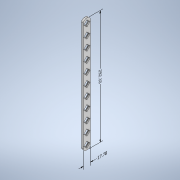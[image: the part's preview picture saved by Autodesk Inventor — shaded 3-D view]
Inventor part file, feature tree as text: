
AUTODESK INVENTOR PART (.ipt)
format: ipt  version: 2020 (Build 240168000, 168)  size: 428,544 bytes
history: native  units: mm
features: chamfer x88, other x3, extrude x2, sketch x2, fillet x1
ambient origin geometry x8: Origin, YZ Plane, XZ Plane, XY Plane, X Axis, Y Axis, Z Axis, Center Point
bodies: Solid1 (feature_tree)
feature tree (96):
  other  "Annotations"
  extrude  "Extrusion1"  Depth=17.78mm
  extrude  "Extrusion2"  Depth=5.0mm TaperAngle=0.0deg
  fillet  "Fillet1"  Radius=7.0mm
  chamfer  "Chamfer1"  Distance=1.0mm Angle=45.0deg
  chamfer  "Chamfer2"  Distance=1.0mm Angle=45.0deg
  chamfer  "Chamfer3"  Distance=1.0mm Angle=45.0deg
  chamfer  "Chamfer4"  Distance=1.0mm Angle=45.0deg
  chamfer  "Chamfer5"  Distance=1.0mm Angle=45.0deg
  chamfer  "Chamfer6"  Distance=1.0mm Angle=45.0deg
  chamfer  "Chamfer7"  Distance=1.0mm Angle=45.0deg
  chamfer  "Chamfer8"  Distance=1.0mm Angle=45.0deg
  chamfer  "Chamfer9"  Distance=1.0mm Angle=45.0deg
  chamfer  "Chamfer10"  Distance=1.0mm Angle=45.0deg
  chamfer  "Chamfer11"  Distance=1.0mm Angle=45.0deg
  chamfer  "Chamfer12"  Distance=1.0mm Angle=45.0deg
  chamfer  "Chamfer13"  Distance=1.0mm Angle=45.0deg
  chamfer  "Chamfer14"  Distance=1.0mm Angle=45.0deg
  chamfer  "Chamfer15"  Distance=1.0mm Angle=45.0deg
  chamfer  "Chamfer16"  Distance=1.0mm Angle=45.0deg
  chamfer  "Chamfer17"  Distance=1.0mm Angle=45.0deg
  chamfer  "Chamfer18"  Distance=1.0mm Angle=45.0deg
  chamfer  "Chamfer19"  Distance=1.0mm Angle=45.0deg
  chamfer  "Chamfer20"  Distance=1.0mm Angle=45.0deg
  chamfer  "Chamfer21"  Distance=1.0mm Angle=45.0deg
  chamfer  "Chamfer22"  Distance=1.0mm Angle=45.0deg
  chamfer  "Chamfer23"  Distance=1.0mm Angle=45.0deg
  chamfer  "Chamfer24"  Distance=1.0mm Angle=45.0deg
  chamfer  "Chamfer25"  Distance=1.0mm Angle=45.0deg
  chamfer  "Chamfer26"  Distance=1.0mm Angle=45.0deg
  chamfer  "Chamfer27"  Distance=1.0mm Angle=45.0deg
  chamfer  "Chamfer28"  Distance=1.0mm Angle=45.0deg
  chamfer  "Chamfer29"  Distance=1.0mm Angle=45.0deg
  chamfer  "Chamfer30"  Distance=1.0mm Angle=45.0deg
  chamfer  "Chamfer31"  Distance=1.0mm Angle=45.0deg
  chamfer  "Chamfer32"  Distance=1.0mm Angle=45.0deg
  chamfer  "Chamfer33"  Distance=1.0mm Angle=45.0deg
  chamfer  "Chamfer34"  Distance=1.0mm Angle=45.0deg
  chamfer  "Chamfer35"  Distance=1.0mm Angle=45.0deg
  chamfer  "Chamfer36"  Distance=1.0mm Angle=45.0deg
  chamfer  "Chamfer37"  Distance=1.0mm Angle=45.0deg
  chamfer  "Chamfer38"  Distance=1.0mm Angle=45.0deg
  chamfer  "Chamfer39"  Distance=1.0mm Angle=45.0deg
  chamfer  "Chamfer40"  Distance=1.0mm Angle=45.0deg
  chamfer  "Chamfer41"  Distance=1.0mm Angle=45.0deg
  chamfer  "Chamfer42"  Distance=1.0mm Angle=45.0deg
  chamfer  "Chamfer43"  Distance=1.0mm Angle=45.0deg
  chamfer  "Chamfer44"  Distance=1.0mm Angle=45.0deg
  chamfer  "Chamfer45"  Distance=1.0mm Angle=45.0deg
  chamfer  "Chamfer46"  Distance=1.0mm Angle=45.0deg
  chamfer  "Chamfer47"  Distance=1.0mm Angle=45.0deg
  chamfer  "Chamfer48"  Distance=1.0mm Angle=45.0deg
  chamfer  "Chamfer49"  Distance=1.0mm Angle=45.0deg
  chamfer  "Chamfer50"  Distance=1.0mm Angle=45.0deg
  chamfer  "Chamfer51"  Distance=1.0mm Angle=45.0deg
  chamfer  "Chamfer52"  Distance=1.0mm Angle=45.0deg
  chamfer  "Chamfer53"  Distance=1.0mm Angle=45.0deg
  chamfer  "Chamfer54"  Distance=1.0mm Angle=45.0deg
  chamfer  "Chamfer55"  Distance=1.0mm Angle=45.0deg
  chamfer  "Chamfer56"  Distance=1.0mm Angle=45.0deg
  chamfer  "Chamfer57"  Distance=1.0mm Angle=45.0deg
  chamfer  "Chamfer58"  Distance=1.0mm Angle=45.0deg
  chamfer  "Chamfer59"  Distance=1.0mm Angle=45.0deg
  chamfer  "Chamfer60"  Distance=1.0mm Angle=45.0deg
  chamfer  "Chamfer61"  Distance=1.0mm Angle=45.0deg
  chamfer  "Chamfer62"  Distance=1.0mm Angle=45.0deg
  chamfer  "Chamfer63"  Distance=1.0mm Angle=45.0deg
  chamfer  "Chamfer64"  Distance=1.0mm Angle=45.0deg
  chamfer  "Chamfer65"  Distance=1.0mm Angle=45.0deg
  chamfer  "Chamfer66"  Distance=1.0mm Angle=45.0deg
  chamfer  "Chamfer67"  Distance=1.0mm Angle=45.0deg
  chamfer  "Chamfer68"  Distance=1.0mm Angle=45.0deg
  chamfer  "Chamfer69"  Distance=1.0mm Angle=45.0deg
  chamfer  "Chamfer70"  Distance=1.0mm Angle=45.0deg
  chamfer  "Chamfer71"  Distance=1.0mm Angle=45.0deg
  chamfer  "Chamfer72"  Distance=1.0mm Angle=45.0deg
  chamfer  "Chamfer73"  Distance=1.0mm Angle=45.0deg
  chamfer  "Chamfer74"  Distance=1.0mm Angle=45.0deg
  chamfer  "Chamfer75"  Distance=1.0mm Angle=45.0deg
  chamfer  "Chamfer76"  Distance=1.0mm Angle=45.0deg
  chamfer  "Chamfer77"  Distance=1.0mm Angle=45.0deg
  chamfer  "Chamfer78"  Distance=1.0mm Angle=45.0deg
  chamfer  "Chamfer79"  Distance=1.0mm Angle=45.0deg
  chamfer  "Chamfer80"  Distance=1.0mm Angle=45.0deg
  chamfer  "Chamfer81"  Distance=1.0mm Angle=45.0deg
  chamfer  "Chamfer82"  Distance=1.0mm Angle=45.0deg
  chamfer  "Chamfer83"  Distance=1.0mm Angle=45.0deg
  chamfer  "Chamfer84"  Distance=1.0mm Angle=45.0deg
  chamfer  "Chamfer85"  Distance=1.0mm Angle=45.0deg
  chamfer  "Chamfer86"  Distance=1.0mm Angle=45.0deg
  chamfer  "Chamfer87"  Distance=1.0mm Angle=45.0deg
  chamfer  "Chamfer88"  Distance=1.0mm Angle=45.0deg
  sketch  "Sketch1"  dims[d0=292.1mm d1=17.78mm]
  sketch  "Sketch2"  dims[d2=5.0mm d3=0.0mm d15=5.0mm d16=0.0mm d17=7.0mm d18=1.0mm d19=2.0mm d20=45.0deg d21=1.0mm d22=2.0mm d23=45.0deg d24=1.0mm d25=2.0mm d26=45.0deg d27=1.0mm d28=2.0mm d29=45.0deg d30=1.0mm d31=2.0mm d32=45.0deg d33=1.0mm d34=2.0mm d35=45.0deg d36=1.0mm d37=2.0mm d38=45.0deg d39=1.0mm d40=2.0mm d41=45.0deg d42=1.0mm d43=2.0mm d44=45.0deg d45=1.0mm d46=2.0mm d47=45.0deg d48=1.0mm d49=2.0mm d50=45.0deg d51=1.0mm d52=2.0mm d53=45.0deg d54=1.0mm d55=2.0mm d56=45.0deg d57=1.0mm d58=2.0mm d59=45.0deg d60=1.0mm d61=2.0mm d62=45.0deg d63=1.0mm d64=2.0mm d65=45.0deg d66=1.0mm d67=2.0mm d68=45.0deg d69=1.0mm d70=2.0mm d71=45.0deg d72=1.0mm d73=2.0mm d74=45.0deg d75=1.0mm d76=2.0mm d77=45.0deg d78=1.0mm d79=2.0mm d80=45.0deg d81=1.0mm d82=2.0mm d83=45.0deg d84=1.0mm d85=2.0mm d86=45.0deg d87=1.0mm d88=2.0mm d89=45.0deg d90=1.0mm d91=2.0mm d92=45.0deg d93=1.0mm d94=2.0mm d95=45.0deg d96=1.0mm d97=2.0mm d98=45.0deg d99=1.0mm d100=2.0mm d101=45.0deg d102=1.0mm d103=2.0mm d104=45.0deg d105=1.0mm d106=2.0mm d107=45.0deg d108=1.0mm d109=2.0mm d110=45.0deg d111=1.0mm d112=2.0mm d113=45.0deg d114=1.0mm d115=2.0mm d116=45.0deg d117=1.0mm d118=2.0mm d119=45.0deg d120=1.0mm d121=2.0mm d122=45.0deg d123=1.0mm d124=2.0mm d125=45.0deg d126=1.0mm d127=2.0mm d128=45.0deg d129=1.0mm d130=2.0mm d131=45.0deg d132=1.0mm d133=2.0mm d134=45.0deg d135=1.0mm d136=2.0mm d137=45.0deg d138=1.0mm d139=2.0mm d140=45.0deg d141=1.0mm d142=2.0mm d143=45.0deg d144=1.0mm d145=2.0mm d146=45.0deg d147=1.0mm d148=2.0mm d149=45.0deg d150=1.0mm d151=2.0mm d152=45.0deg d153=1.0mm d154=2.0mm d155=45.0deg d156=1.0mm d157=2.0mm d158=45.0deg d159=1.0mm d160=2.0mm d161=45.0deg d162=1.0mm d163=2.0mm d164=45.0deg d165=1.0mm d166=2.0mm d167=45.0deg d168=1.0mm d169=2.0mm d170=45.0deg d171=1.0mm d172=2.0mm d173=45.0deg d174=1.0mm d175=2.0mm d176=45.0deg d177=1.0mm d178=2.0mm d179=45.0deg d180=1.0mm d181=2.0mm d182=45.0deg d183=1.0mm d184=2.0mm d185=45.0deg d186=1.0mm d187=2.0mm d188=45.0deg d189=1.0mm d190=2.0mm d191=45.0deg d192=1.0mm d193=2.0mm d194=45.0deg d195=1.0mm d196=2.0mm d197=45.0deg d198=1.0mm d199=2.0mm d200=45.0deg d201=1.0mm d202=2.0mm d203=45.0deg d204=1.0mm d205=2.0mm d206=45.0deg d207=1.0mm d208=2.0mm d209=45.0deg d210=1.0mm d211=2.0mm d212=45.0deg d213=1.0mm d214=2.0mm d215=45.0deg d216=1.0mm d217=2.0mm d218=45.0deg d219=1.0mm d220=2.0mm d221=45.0deg d222=1.0mm d223=2.0mm d224=45.0deg d225=1.0mm d226=2.0mm d227=45.0deg d228=1.0mm d229=2.0mm d230=45.0deg d231=1.0mm d232=2.0mm d233=45.0deg d234=1.0mm d235=2.0mm d236=45.0deg d237=1.0mm d238=2.0mm d239=45.0deg d240=1.0mm d241=2.0mm d242=45.0deg d243=1.0mm d244=2.0mm d245=45.0deg d246=1.0mm d247=2.0mm d248=45.0deg d249=1.0mm d250=2.0mm d251=45.0deg d252=1.0mm d253=2.0mm d254=45.0deg d255=1.0mm d256=2.0mm d257=45.0deg d258=1.0mm d259=2.0mm d260=45.0deg d261=1.0mm d262=2.0mm d263=45.0deg d264=1.0mm d265=2.0mm d266=45.0deg d267=1.0mm d268=2.0mm d269=45.0deg d270=1.0mm d271=2.0mm d272=45.0deg d273=1.0mm d274=2.0mm d275=45.0deg d276=1.0mm d277=2.0mm d278=45.0deg d279=1.0mm d280=2.0mm d281=45.0deg d282=4.961605mm d283=5.41079mm d284=292.1mm d285=5.428365mm d286=4.571635mm d287=17.78mm]
  other  "Linear Dimension 1"
  other  "Linear Dimension 2"
